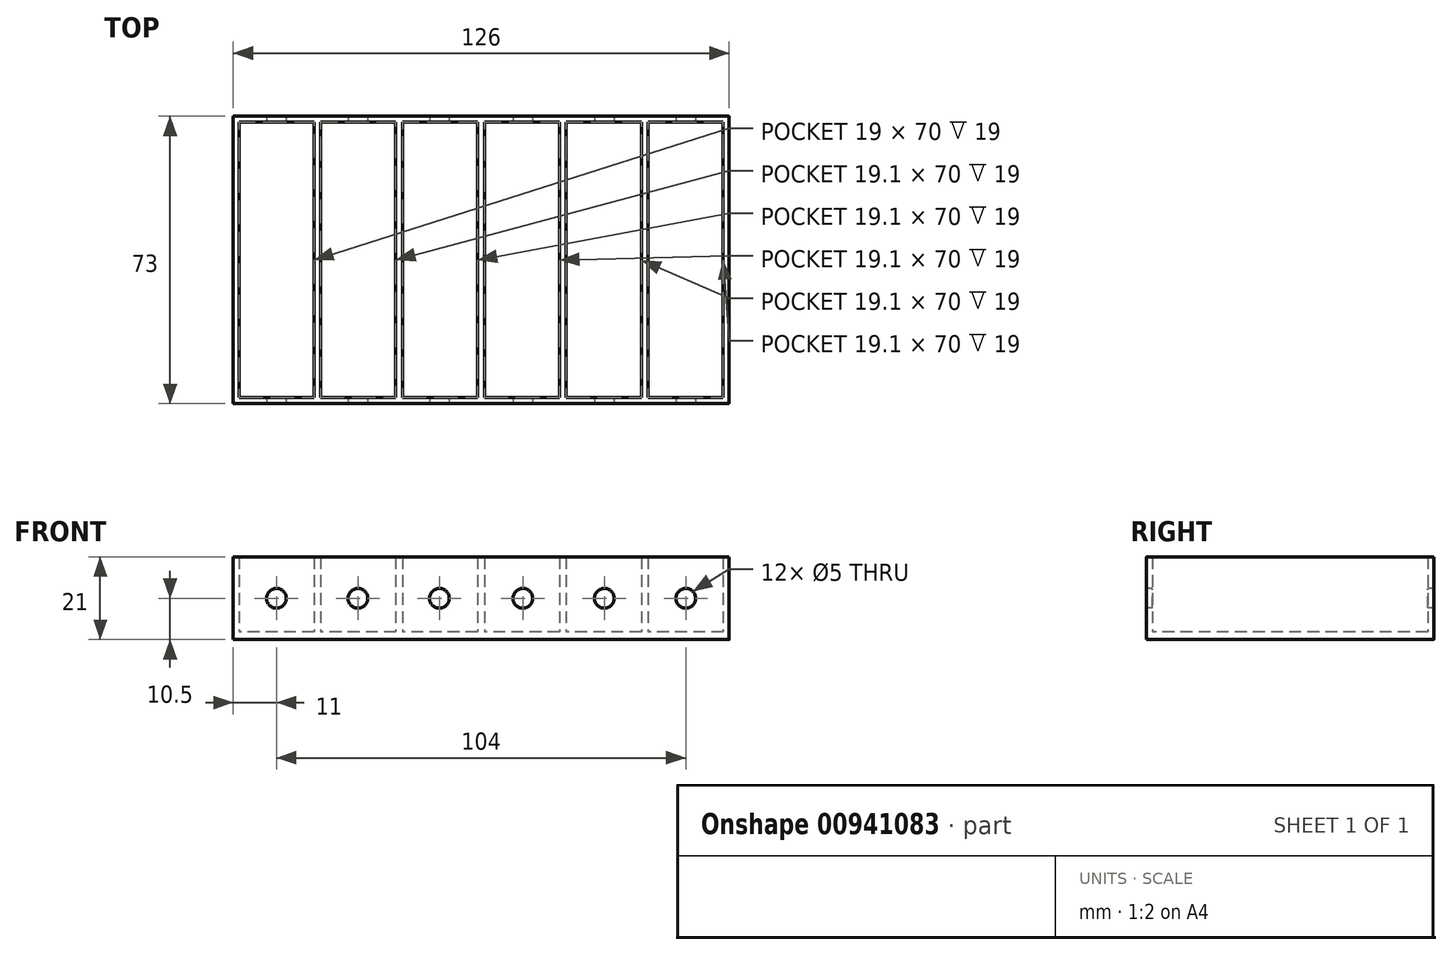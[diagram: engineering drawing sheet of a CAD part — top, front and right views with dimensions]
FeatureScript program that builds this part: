
annotation { "Feature Type Name" : "Feature", "Feature Type Description" : "" }
export const myFeature = defineFeature(function(context is Context, id is Id, definition is map)
    precondition{}
    {
        {
            var Q0;
            Q0=qCreatedBy(makeId("Top.planeOp"),FACE);
            var sketch = newSketch(context, id + "F0", { "sketchPlane" : qUnion([Q0]), "disableImprinting" : false});
            skLineSegment(sketch, "E0.bottom", {"start": v(63, 36.5) * mm, "end": v(-63, 36.5) * mm});
            skLineSegment(sketch, "E0.top", {"start": v(63, -36.5) * mm, "end": v(-63, -36.5) * mm});
            skLineSegment(sketch, "E0.left", {"start": v(63, 36.5) * mm, "end": v(63, -36.5) * mm});
            skLineSegment(sketch, "E0.right", {"start": v(-63, 36.5) * mm, "end": v(-63, -36.5) * mm});
            skPoint(sketch, "E0.middle", {"position": v(0, 0) * mm});
            skSolve(sketch);
        }
        {
            var Q0;
            Q0=qSketchRegion(id+"F0",true);
            extrude(context, id + "F1", {"entities" : qUnion([Q0]), "depth" : 2 * mm, "offsetDistance" : 25 * mm});
        }
        {
            var Q0;
            Q0=makeQuery(id+"F1.opExtrude","CAP_FACE",FACE,{"disambiguationData":[OSD([sQuery(id+"F0.wireOp",EDGE,"E0.bottom"),sQuery(id+"F0.wireOp",EDGE,"E0.top"),sQuery(id+"F0.wireOp",EDGE,"E0.left"),sQuery(id+"F0.wireOp",EDGE,"E0.right")])],"isStart":false});
            var sketch = newSketch(context, id + "F2", { "sketchPlane" : qUnion([Q0]), "disableImprinting" : false});
            skLineSegment(sketch, "E1.0", {"start": v(61.5, 35) * mm, "end": v(-61.5, 35) * mm});
            skLineSegment(sketch, "E1.1", {"start": v(61.5, 35) * mm, "end": v(61.5, -35) * mm});
            skLineSegment(sketch, "E1.2", {"start": v(61.5, -35) * mm, "end": v(-61.5, -35) * mm});
            skLineSegment(sketch, "E1.3", {"start": v(-61.5, 35) * mm, "end": v(-61.5, -35) * mm});
            skLineSegment(sketch, "E2.0", {"start": v(63, 36.5) * mm, "end": v(-63, 36.5) * mm});
            skLineSegment(sketch, "E2.1", {"start": v(63, 36.5) * mm, "end": v(63, -36.5) * mm});
            skLineSegment(sketch, "E2.2", {"start": v(63, -36.5) * mm, "end": v(-63, -36.5) * mm});
            skLineSegment(sketch, "E2.3", {"start": v(-63, 36.5) * mm, "end": v(-63, -36.5) * mm});
            skLineSegment(sketch, "E3.0", {"start": v(-42.5, 37.5) * mm, "end": v(-42.5, -37.5) * mm});
            skLineSegment(sketch, "E4.0", {"start": v(-40.8, 37.5) * mm, "end": v(-40.8, -37.5) * mm});
            skLineSegment(sketch, "E5.0", {"start": v(42.4, 37.5) * mm, "end": v(42.4, -37.5) * mm});
            skLineSegment(sketch, "E6.0", {"start": v(40.7, 37.5) * mm, "end": v(40.7, -37.5) * mm});
            skLineSegment(sketch, "E7.0", {"start": v(21.6, 37.5) * mm, "end": v(21.6, -37.5) * mm});
            skLineSegment(sketch, "E8.0", {"start": v(19.9, 37.5) * mm, "end": v(19.9, -37.5) * mm});
            skLineSegment(sketch, "E9.0", {"start": v(0.8, 37.5) * mm, "end": v(0.8, -37.5) * mm});
            skLineSegment(sketch, "E10.0", {"start": v(-0.9, 37.5) * mm, "end": v(-0.9, -37.5) * mm});
            skLineSegment(sketch, "E11.0", {"start": v(-20, 37.5) * mm, "end": v(-20, -37.5) * mm});
            skLineSegment(sketch, "E12.0", {"start": v(-21.7, 37.5) * mm, "end": v(-21.7, -37.5) * mm});
            skSolve(sketch);
        }
        {
            var Q0;
            Q0=qSketchRegion(id+"F2",true);
            var Q1;
            {var subQ0=sQuery(id+"F2.wireOp",EDGE,"E3.0");Q1=makeQuery(id+"F2.imprint","IMPRINT",FACE,{"disambiguationData":[TD([[makeQuery(id+"F2.imprint","IMPRINT",EDGE,{"derivedFrom":subQ0}),1.0]])]});}
            var Q2;
            {var subQ0=sQuery(id+"F2.wireOp",EDGE,"E11.0");Q2=makeQuery(id+"F2.imprint","IMPRINT",FACE,{"disambiguationData":[TD([[makeQuery(id+"F2.imprint","IMPRINT",EDGE,{"derivedFrom":subQ0}),-1.0]])]});}
            var Q3;
            {var subQ0=sQuery(id+"F2.wireOp",EDGE,"E9.0");Q3=makeQuery(id+"F2.imprint","IMPRINT",FACE,{"disambiguationData":[TD([[makeQuery(id+"F2.imprint","IMPRINT",EDGE,{"derivedFrom":subQ0}),-1.0]])]});}
            var Q4;
            {var subQ0=sQuery(id+"F2.wireOp",EDGE,"E7.0");Q4=makeQuery(id+"F2.imprint","IMPRINT",FACE,{"disambiguationData":[TD([[makeQuery(id+"F2.imprint","IMPRINT",EDGE,{"derivedFrom":subQ0}),-1.0]])]});}
            var Q5;
            {var subQ0=sQuery(id+"F2.wireOp",EDGE,"E5.0");Q5=makeQuery(id+"F2.imprint","IMPRINT",FACE,{"disambiguationData":[TD([[makeQuery(id+"F2.imprint","IMPRINT",EDGE,{"derivedFrom":subQ0}),-1.0]])]});}
            extrude(context, id + "F3", {"entities" : qUnion([Q0, Q1, Q2, Q3, Q4, Q5]), "operationType" : NewBodyOperationType.ADD, "depth" : 19 * mm, "offsetDistance" : 25 * mm});
        }
        {
            var Q0;
            Q0=makeQuery(id+"F3.boolean.opBoolean","MERGE",FACE,{"derivedFrom":[makeQuery(id+"F1.opExtrude","SWEPT_FACE",FACE,{"disambiguationData":[OSD([sQuery(id+"F0.wireOp",EDGE,"E0.top")])]}),makeQuery(id+"F3.opExtrude","SWEPT_FACE",FACE,{"disambiguationData":[OSD([sQuery(id+"F2.wireOp",EDGE,"E2.2")])]})]});
            var sketch = newSketch(context, id + "F4", { "sketchPlane" : qUnion([Q0])});
            skLineSegment(sketch, "E13", {"start": v(-63, 10.5) * mm, "end": v(63, 10.5) * mm});
            skCircle(sketch, "E14", {"center": v(-52, 10.5) * mm, "radius": 2.5 * mm});
            skCircle(sketch, "E15", {"center": v(-31.3, 10.5) * mm, "radius": 2.5 * mm});
            skCircle(sketch, "E16", {"center": v(-10.6, 10.5) * mm, "radius": 2.5 * mm});
            skCircle(sketch, "E17.MirrorC", {"center": v(10.6, 10.5) * mm, "radius": 2.5 * mm});
            skCircle(sketch, "E18.MirrorC", {"center": v(31.3, 10.5) * mm, "radius": 2.5 * mm});
            skCircle(sketch, "E19.MirrorC", {"center": v(52, 10.5) * mm, "radius": 2.5 * mm});
            skSolve(sketch);
        }
        {
            var Q0;
            Q0=qSketchRegion(id+"F4",true);
            extrude(context, id + "F5", {"entities" : qUnion([Q0]), "operationType" : NewBodyOperationType.REMOVE, "oppositeDirection" : true, "depth" : 100 * mm, "offsetDistance" : 25 * mm});
        }
        {
            var Q0;
            Q0=makeQuery(id+"F3.boolean.opBoolean","MERGE",EDGE,{"derivedFrom":[makeQuery(id+"F1.opExtrude","SWEPT_EDGE",EDGE,{"disambiguationData":[OSD([sQuery(id+"F0.wireOp",EDGE,"E0.top"),sQuery(id+"F0.wireOp",EDGE,"E0.right")])]}),makeQuery(id+"F3.opExtrude","SWEPT_EDGE",EDGE,{"disambiguationData":[OSD([sQuery(id+"F2.wireOp",EDGE,"E2.2"),sQuery(id+"F2.wireOp",EDGE,"E2.3")])]})]});
            var Q1;
            Q1=makeQuery(id+"F3.boolean.opBoolean","MERGE",EDGE,{"derivedFrom":[makeQuery(id+"F1.opExtrude","SWEPT_EDGE",EDGE,{"disambiguationData":[OSD([sQuery(id+"F0.wireOp",EDGE,"E0.top"),sQuery(id+"F0.wireOp",EDGE,"E0.left")])]}),makeQuery(id+"F3.opExtrude","SWEPT_EDGE",EDGE,{"disambiguationData":[OSD([sQuery(id+"F2.wireOp",EDGE,"E2.1"),sQuery(id+"F2.wireOp",EDGE,"E2.2")])]})]});
            var Q2;
            Q2=makeQuery(id+"F3.boolean.opBoolean","MERGE",EDGE,{"derivedFrom":[makeQuery(id+"F1.opExtrude","SWEPT_EDGE",EDGE,{"disambiguationData":[OSD([sQuery(id+"F0.wireOp",EDGE,"E0.bottom"),sQuery(id+"F0.wireOp",EDGE,"E0.left")])]}),makeQuery(id+"F3.opExtrude","SWEPT_EDGE",EDGE,{"disambiguationData":[OSD([sQuery(id+"F2.wireOp",EDGE,"E2.0"),sQuery(id+"F2.wireOp",EDGE,"E2.1")])]})]});
            var Q3;
            Q3=makeQuery(id+"F3.boolean.opBoolean","MERGE",EDGE,{"derivedFrom":[makeQuery(id+"F1.opExtrude","SWEPT_EDGE",EDGE,{"disambiguationData":[OSD([sQuery(id+"F0.wireOp",EDGE,"E0.bottom"),sQuery(id+"F0.wireOp",EDGE,"E0.right")])]}),makeQuery(id+"F3.opExtrude","SWEPT_EDGE",EDGE,{"disambiguationData":[OSD([sQuery(id+"F2.wireOp",EDGE,"E2.0"),sQuery(id+"F2.wireOp",EDGE,"E2.3")])]})]});
            fillet(context, id + "F6", {"entities" : qUnion([Q0, Q1, Q2, Q3]), "radius" : .1 * mm, "tangentPropagation" : true, "allowEdgeOverflow" : false});
        }
    });
